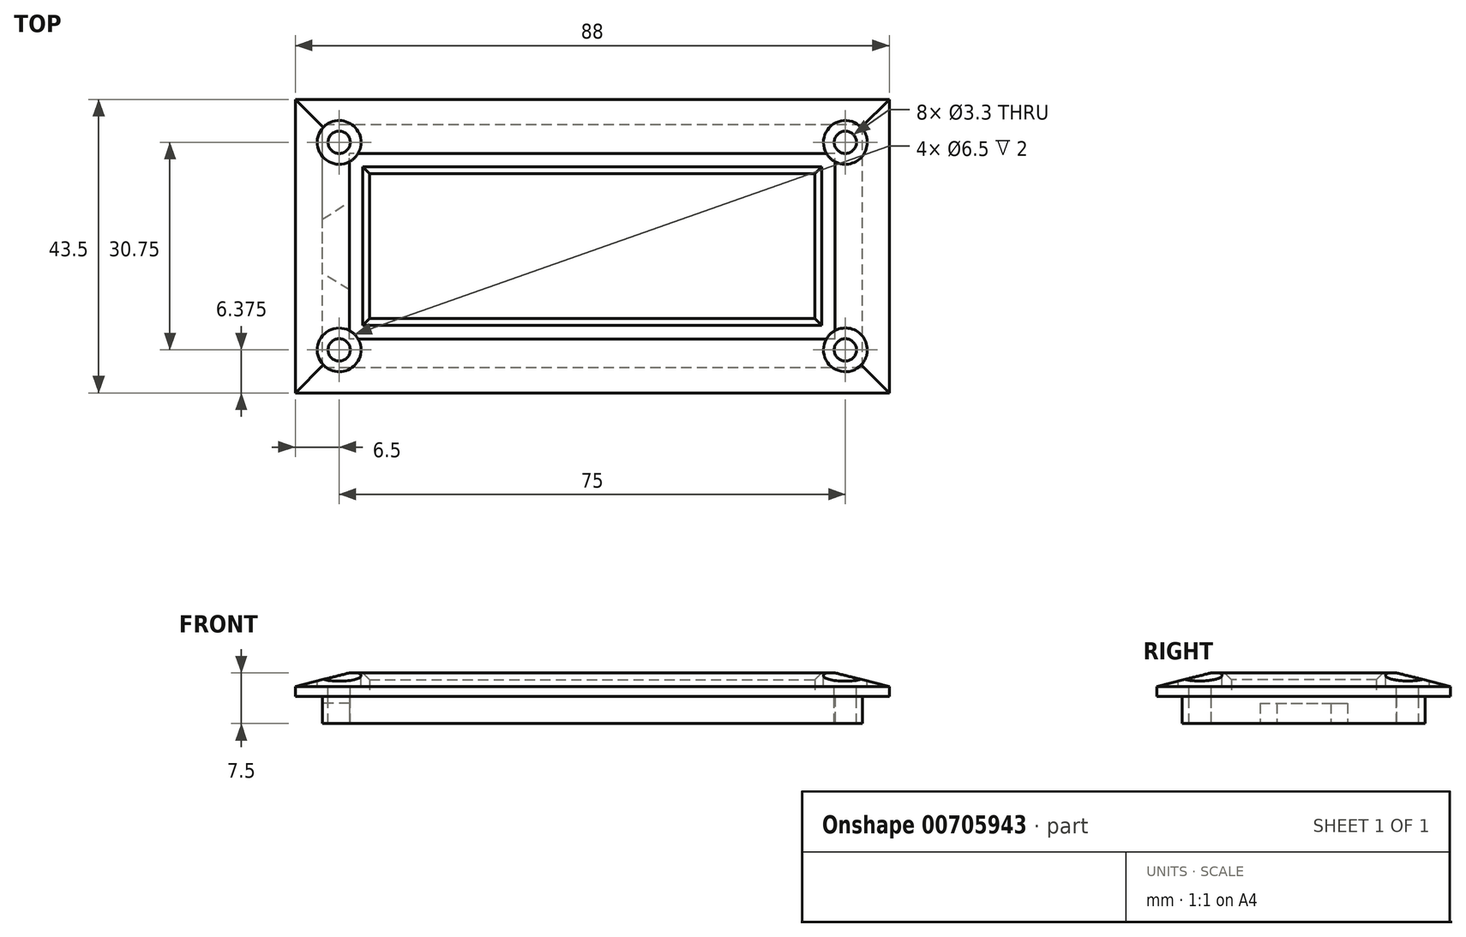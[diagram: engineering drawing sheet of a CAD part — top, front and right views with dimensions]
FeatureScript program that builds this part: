
annotation { "Feature Type Name" : "Feature", "Feature Type Description" : "" }
export const myFeature = defineFeature(function(context is Context, id is Id, definition is map)
    precondition{}
    {
        {
            var Q0;
            Q0=qCreatedBy(makeId("Top.planeOp"),FACE);
            var sketch = newSketch(context, id + "F0", { "sketchPlane" : qUnion([Q0])});
            skLineSegment(sketch, "E0.bottom", {"start": v(36, -13.75) * mm, "end": v(-36, -13.75) * mm});
            skLineSegment(sketch, "E0.top", {"start": v(36, 13.75) * mm, "end": v(-36, 13.75) * mm});
            skLineSegment(sketch, "E0.left", {"start": v(36, -13.75) * mm, "end": v(36, 13.75) * mm});
            skLineSegment(sketch, "E0.right", {"start": v(-36, -13.75) * mm, "end": v(-36, 13.75) * mm});
            skPoint(sketch, "E0.middle", {"position": v(0, 0) * mm});
            skLineSegment(sketch, "E1.bottom", {"start": v(40, -18) * mm, "end": v(-40, -18) * mm});
            skLineSegment(sketch, "E1.top", {"start": v(40, 18) * mm, "end": v(-40, 18) * mm});
            skLineSegment(sketch, "E1.left", {"start": v(40, -18) * mm, "end": v(40, 18) * mm});
            skLineSegment(sketch, "E1.right", {"start": v(-40, -18) * mm, "end": v(-40, 18) * mm});
            skSolve(sketch);
        }
        {
            var Q0;
            Q0=makeQuery(id+"F0.imprint","IMPRINT",FACE,{"disambiguationData":[TD([[makeQuery(id+"F0.imprint","IMPRINT",EDGE,{"derivedFrom":sQuery(id+"F0.wireOp",EDGE,"E0.bottom")}),1.0]])]});
            extrude(context, id + "F1", {"entities" : qUnion([Q0]), "depth" : 4 * mm, "offsetDistance" : 25 * mm});
        }
        {
            var Q0;
            Q0=makeQuery(id+"F1.opExtrude","CAP_FACE",FACE,{"disambiguationData":[OSD([sQuery(id+"F0.wireOp",EDGE,"E0.bottom"),sQuery(id+"F0.wireOp",EDGE,"E0.top"),sQuery(id+"F0.wireOp",EDGE,"E0.left"),sQuery(id+"F0.wireOp",EDGE,"E0.right"),sQuery(id+"F0.wireOp",EDGE,"E1.bottom"),sQuery(id+"F0.wireOp",EDGE,"E1.top"),sQuery(id+"F0.wireOp",EDGE,"E1.left"),sQuery(id+"F0.wireOp",EDGE,"E1.right")])],"isStart":true});
            var sketch = newSketch(context, id + "F2", { "sketchPlane" : qUnion([Q0])});
            skLineSegment(sketch, "E2", {"start": v(-36, 6.5) * mm, "end": v(-40, 4) * mm});
            skLineSegment(sketch, "E3", {"start": v(-40, 4) * mm, "end": v(-40, -4) * mm});
            skLineSegment(sketch, "E4", {"start": v(-40, -4) * mm, "end": v(-36, -6.5) * mm});
            skLineSegment(sketch, "E5", {"start": v(-36, -6.5) * mm, "end": v(-36, 6.5) * mm});
            skSolve(sketch);
        }
        {
            var Q0;
            Q0=makeQuery(id+"F2.imprint","IMPRINT",FACE,{"disambiguationData":[TD([[makeQuery(id+"F2.imprint","IMPRINT",EDGE,{"derivedFrom":sQuery(id+"F2.wireOp",EDGE,"E2")}),1.0]])]});
            extrude(context, id + "F3", {"entities" : qUnion([Q0]), "operationType" : NewBodyOperationType.REMOVE, "oppositeDirection" : true, "depth" : 3 * mm, "offsetDistance" : 25 * mm});
        }
        {
            var Q0;
            Q0=makeQuery(id+"F1.opExtrude","CAP_FACE",FACE,{"disambiguationData":[OSD([sQuery(id+"F0.wireOp",EDGE,"E0.bottom"),sQuery(id+"F0.wireOp",EDGE,"E0.top"),sQuery(id+"F0.wireOp",EDGE,"E0.left"),sQuery(id+"F0.wireOp",EDGE,"E0.right"),sQuery(id+"F0.wireOp",EDGE,"E1.bottom"),sQuery(id+"F0.wireOp",EDGE,"E1.top"),sQuery(id+"F0.wireOp",EDGE,"E1.left"),sQuery(id+"F0.wireOp",EDGE,"E1.right")])],"isStart":false});
            var sketch = newSketch(context, id + "F4", { "sketchPlane" : qUnion([Q0])});
            skLineSegment(sketch, "E6.bottom", {"start": v(37.5, -15.37) * mm, "end": v(-37.5, -15.38) * mm});
            skLineSegment(sketch, "E6.top", {"start": v(37.5, 15.38) * mm, "end": v(-37.5, 15.37) * mm});
            skLineSegment(sketch, "E6.left", {"start": v(37.5, -15.37) * mm, "end": v(37.5, 15.38) * mm});
            skLineSegment(sketch, "E6.right", {"start": v(-37.5, -15.38) * mm, "end": v(-37.5, 15.37) * mm});
            skPoint(sketch, "E6.middle", {"position": v(0, 0) * mm});
            skCircle(sketch, "E7", {"center": v(-37.5, 15.37) * mm, "radius": 1.63 * mm});
            skCircle(sketch, "E8", {"center": v(-37.5, -15.38) * mm, "radius": 1.63 * mm});
            skCircle(sketch, "E9", {"center": v(37.5, -15.37) * mm, "radius": 1.63 * mm});
            skCircle(sketch, "E10", {"center": v(37.5, 15.38) * mm, "radius": 1.63 * mm});
            skSolve(sketch);
        }
        {
            var Q0;
            {var subQ0=sQuery(id+"F4.wireOp",EDGE,"E6.right");var subQ1=sQuery(id+"F4.wireOp",EDGE,"E6.top");var subQ2=makeQuery(id+"F4.imprint","INTERSECT",VERTEX,{"derivedFrom":[subQ1,subQ0]});Q0=makeQuery(id+"F4.imprint","IMPRINT",FACE,{"disambiguationData":[TD([[makeQuery(id+"F4.imprint","IMPRINT",EDGE,{"disambiguationData":[TD([[subQ2,1.0]])],"derivedFrom":subQ1}),1.0]])]});}
            var Q1;
            {var subQ0=sQuery(id+"F4.wireOp",EDGE,"E6.right");var subQ1=sQuery(id+"F4.wireOp",EDGE,"E6.top");var subQ2=makeQuery(id+"F4.imprint","INTERSECT",VERTEX,{"derivedFrom":[subQ1,subQ0]});Q1=makeQuery(id+"F4.imprint","IMPRINT",FACE,{"disambiguationData":[TD([[makeQuery(id+"F4.imprint","IMPRINT",EDGE,{"disambiguationData":[TD([[subQ2,1.0]])],"derivedFrom":subQ1}),-1.0]])]});}
            var Q2;
            {var subQ0=sQuery(id+"F4.wireOp",EDGE,"E6.right");var subQ1=sQuery(id+"F4.wireOp",EDGE,"E6.bottom");var subQ2=makeQuery(id+"F4.imprint","INTERSECT",VERTEX,{"derivedFrom":[subQ1,subQ0]});Q2=makeQuery(id+"F4.imprint","IMPRINT",FACE,{"disambiguationData":[TD([[makeQuery(id+"F4.imprint","IMPRINT",EDGE,{"disambiguationData":[TD([[subQ2,1.0]])],"derivedFrom":subQ1}),1.0]])]});}
            var Q3;
            {var subQ0=sQuery(id+"F4.wireOp",EDGE,"E6.right");var subQ1=sQuery(id+"F4.wireOp",EDGE,"E6.bottom");var subQ2=makeQuery(id+"F4.imprint","INTERSECT",VERTEX,{"derivedFrom":[subQ1,subQ0]});Q3=makeQuery(id+"F4.imprint","IMPRINT",FACE,{"disambiguationData":[TD([[makeQuery(id+"F4.imprint","IMPRINT",EDGE,{"disambiguationData":[TD([[subQ2,1.0]])],"derivedFrom":subQ1}),-1.0]])]});}
            var Q4;
            {var subQ0=sQuery(id+"F4.wireOp",EDGE,"E6.left");var subQ1=sQuery(id+"F4.wireOp",EDGE,"E6.bottom");var subQ2=makeQuery(id+"F4.imprint","INTERSECT",VERTEX,{"derivedFrom":[subQ1,subQ0]});Q4=makeQuery(id+"F4.imprint","IMPRINT",FACE,{"disambiguationData":[TD([[makeQuery(id+"F4.imprint","IMPRINT",EDGE,{"disambiguationData":[TD([[subQ2,-1.0]])],"derivedFrom":subQ1}),1.0]])]});}
            var Q5;
            {var subQ0=sQuery(id+"F4.wireOp",EDGE,"E6.left");var subQ1=sQuery(id+"F4.wireOp",EDGE,"E6.bottom");var subQ2=makeQuery(id+"F4.imprint","INTERSECT",VERTEX,{"derivedFrom":[subQ1,subQ0]});Q5=makeQuery(id+"F4.imprint","IMPRINT",FACE,{"disambiguationData":[TD([[makeQuery(id+"F4.imprint","IMPRINT",EDGE,{"disambiguationData":[TD([[subQ2,-1.0]])],"derivedFrom":subQ1}),-1.0]])]});}
            var Q6;
            {var subQ0=sQuery(id+"F4.wireOp",EDGE,"E6.left");var subQ1=sQuery(id+"F4.wireOp",EDGE,"E6.top");var subQ2=makeQuery(id+"F4.imprint","INTERSECT",VERTEX,{"derivedFrom":[subQ1,subQ0]});Q6=makeQuery(id+"F4.imprint","IMPRINT",FACE,{"disambiguationData":[TD([[makeQuery(id+"F4.imprint","IMPRINT",EDGE,{"disambiguationData":[TD([[subQ2,-1.0]])],"derivedFrom":subQ1}),1.0]])]});}
            var Q7;
            {var subQ0=sQuery(id+"F4.wireOp",EDGE,"E6.left");var subQ1=sQuery(id+"F4.wireOp",EDGE,"E6.top");var subQ2=makeQuery(id+"F4.imprint","INTERSECT",VERTEX,{"derivedFrom":[subQ1,subQ0]});Q7=makeQuery(id+"F4.imprint","IMPRINT",FACE,{"disambiguationData":[TD([[makeQuery(id+"F4.imprint","IMPRINT",EDGE,{"disambiguationData":[TD([[subQ2,-1.0]])],"derivedFrom":subQ1}),-1.0]])]});}
            var Q8;
            Q8=sQuery(id+"F4.wireOp",EDGE,"E7");
            var Q9;
            Q9=sQuery(id+"F4.wireOp",EDGE,"E8");
            var Q10;
            Q10=sQuery(id+"F4.wireOp",EDGE,"E9");
            var Q11;
            Q11=sQuery(id+"F4.wireOp",EDGE,"E10");
            extrude(context, id + "F5", {"entities" : qUnion([Q0, Q1, Q2, Q3, Q4, Q5, Q6, Q7]), "surfaceEntities" : qUnion([Q8, Q9, Q10, Q11]), "endBound" : BoundingType.SYMMETRIC, "depth" : 50 * mm, "offsetDistance" : 25 * mm});
        }
        {
            var Q0;
            Q0=makeQuery(id+"F1.opExtrude","CAP_FACE",FACE,{"disambiguationData":[OSD([sQuery(id+"F0.wireOp",EDGE,"E0.bottom"),sQuery(id+"F0.wireOp",EDGE,"E0.top"),sQuery(id+"F0.wireOp",EDGE,"E0.left"),sQuery(id+"F0.wireOp",EDGE,"E0.right"),sQuery(id+"F0.wireOp",EDGE,"E1.bottom"),sQuery(id+"F0.wireOp",EDGE,"E1.top"),sQuery(id+"F0.wireOp",EDGE,"E1.left"),sQuery(id+"F0.wireOp",EDGE,"E1.right")])],"isStart":false});
            var sketch = newSketch(context, id + "F6", { "sketchPlane" : qUnion([Q0])});
            skLineSegment(sketch, "E11.0", {"start": v(44, -21.75) * mm, "end": v(44, 21.75) * mm});
            skLineSegment(sketch, "E11.1", {"start": v(44, -21.75) * mm, "end": v(-44, -21.75) * mm});
            skLineSegment(sketch, "E11.2", {"start": v(-44, -21.75) * mm, "end": v(-44, 21.75) * mm});
            skLineSegment(sketch, "E11.3", {"start": v(44, 21.75) * mm, "end": v(-44, 21.75) * mm});
            skLineSegment(sketch, "E12.0", {"start": v(-33, -10.75) * mm, "end": v(-33, 10.75) * mm});
            skLineSegment(sketch, "E12.1", {"start": v(33, -10.75) * mm, "end": v(-33, -10.75) * mm});
            skLineSegment(sketch, "E12.2", {"start": v(33, -10.75) * mm, "end": v(33, 10.75) * mm});
            skLineSegment(sketch, "E12.3", {"start": v(33, 10.75) * mm, "end": v(-33, 10.75) * mm});
            skPoint(sketch, "E13.0.end.orphan", {"position": v(-36, 13.75) * mm});
            skPoint(sketch, "E14.0.end.orphan", {"position": v(-36, -13.75) * mm});
            skPoint(sketch, "E15.0.end.orphan", {"position": v(36, 13.75) * mm});
            skPoint(sketch, "E15.0.start.orphan", {"position": v(36, -13.75) * mm});
            skSolve(sketch);
        }
        {
            var Q0;
            Q0=makeQuery(id+"F6.imprint","IMPRINT",FACE,{"disambiguationData":[TD([[makeQuery(id+"F6.imprint","IMPRINT",EDGE,{"derivedFrom":sQuery(id+"F6.wireOp",EDGE,"E11.0")}),1.0]])]});
            var Q1;
            Q1=makeQuery(id+"F6.imprint","IMPRINT",FACE,{"disambiguationData":[TD([[makeQuery(id+"F6.imprint","IMPRINT",EDGE,{"derivedFrom":makeQuery(id+"F1.opExtrude","CAP_EDGE",EDGE,{"disambiguationData":[OSD([sQuery(id+"F0.wireOp",EDGE,"E0.bottom")])],"isStart":false})}),1.0]])]});
            var Q2;
            Q2=makeQuery(id+"F6.imprint","IMPRINT",FACE,{"disambiguationData":[TD([[makeQuery(id+"F6.imprint","IMPRINT",EDGE,{"derivedFrom":sQuery(id+"F6.wireOp",EDGE,"E12.0")}),1.0]])]});
            extrude(context, id + "F7", {"entities" : qUnion([Q0, Q1, Q2]), "depth" : 3.5 * mm, "offsetDistance" : 25 * mm});
        }
        {
            var Q0;
            Q0=makeQuery(id+"F7.opExtrude","CAP_EDGE",EDGE,{"disambiguationData":[OSD([sQuery(id+"F6.wireOp",EDGE,"E11.1")])],"isStart":false});
            var Q1;
            Q1=makeQuery(id+"F7.opExtrude","CAP_EDGE",EDGE,{"disambiguationData":[OSD([sQuery(id+"F6.wireOp",EDGE,"E11.2")])],"isStart":false});
            var Q2;
            Q2=makeQuery(id+"F7.opExtrude","CAP_EDGE",EDGE,{"disambiguationData":[OSD([sQuery(id+"F6.wireOp",EDGE,"E11.3")])],"isStart":false});
            var Q3;
            Q3=makeQuery(id+"F7.opExtrude","CAP_EDGE",EDGE,{"disambiguationData":[OSD([sQuery(id+"F6.wireOp",EDGE,"E11.0")])],"isStart":false});
            chamfer(context, id + "F8", {"entities" : qUnion([Q0, Q1, Q2, Q3]), "chamferType" : ChamferType.TWO_OFFSETS, "width1" : 2 * mm, "oppositeDirection" : false, "width2" : 8 * mm, "tangentPropagation" : true});
        }
        {
            var Q0;
            Q0=makeQuery(id+"F7.opExtrude","CAP_EDGE",EDGE,{"disambiguationData":[OSD([sQuery(id+"F6.wireOp",EDGE,"E12.0")])],"isStart":false});
            var Q1;
            Q1=makeQuery(id+"F7.opExtrude","CAP_EDGE",EDGE,{"disambiguationData":[OSD([sQuery(id+"F6.wireOp",EDGE,"E12.3")])],"isStart":false});
            var Q2;
            Q2=makeQuery(id+"F7.opExtrude","CAP_EDGE",EDGE,{"disambiguationData":[OSD([sQuery(id+"F6.wireOp",EDGE,"E12.2")])],"isStart":false});
            var Q3;
            Q3=makeQuery(id+"F7.opExtrude","CAP_EDGE",EDGE,{"disambiguationData":[OSD([sQuery(id+"F6.wireOp",EDGE,"E12.1")])],"isStart":false});
            chamfer(context, id + "F9", {"entities" : qUnion([Q0, Q1, Q2, Q3]), "width" : 1 * mm, "tangentPropagation" : true});
        }
        {
            var Q0;
            Q0=makeQuery(id+"F7.opExtrude","CAP_FACE",FACE,{"disambiguationData":[OSD([sQuery(id+"F6.wireOp",EDGE,"E11.0"),sQuery(id+"F6.wireOp",EDGE,"E11.1"),sQuery(id+"F6.wireOp",EDGE,"E11.2"),sQuery(id+"F6.wireOp",EDGE,"E11.3"),sQuery(id+"F6.wireOp",EDGE,"E12.0"),sQuery(id+"F6.wireOp",EDGE,"E12.1"),sQuery(id+"F6.wireOp",EDGE,"E12.2"),sQuery(id+"F6.wireOp",EDGE,"E12.3")])],"isStart":false});
            var sketch = newSketch(context, id + "F10", { "sketchPlane" : qUnion([Q0])});
            skPoint(sketch, "E16.0", {"position": v(-37.5, 15.37) * mm});
            skPoint(sketch, "E17.0", {"position": v(-37.5, -15.38) * mm});
            skPoint(sketch, "E18.0", {"position": v(37.5, -15.37) * mm});
            skPoint(sketch, "E19.0", {"position": v(37.5, 15.38) * mm});
            skSolve(sketch);
        }
        {
            var Q0;
            Q0=sQuery(id+"F10.wireOp",VERTEX,"E19.0");
            var Q1;
            Q1=sQuery(id+"F10.wireOp",VERTEX,"E18.0");
            var Q2;
            Q2=sQuery(id+"F10.wireOp",VERTEX,"E17.0");
            var Q3;
            Q3=sQuery(id+"F10.wireOp",VERTEX,"E16.0");
            var Q4;
            Q4=makeQuery(id+"F1.opExtrude","SWEPT_BODY",BODY,{"disambiguationData":[OSD([sQuery(id+"F0.wireOp",EDGE,"E0.bottom"),sQuery(id+"F0.wireOp",EDGE,"E0.top"),sQuery(id+"F0.wireOp",EDGE,"E0.left"),sQuery(id+"F0.wireOp",EDGE,"E0.right"),sQuery(id+"F0.wireOp",EDGE,"E1.bottom"),sQuery(id+"F0.wireOp",EDGE,"E1.top"),sQuery(id+"F0.wireOp",EDGE,"E1.left"),sQuery(id+"F0.wireOp",EDGE,"E1.right")])]});
            var Q5;
            Q5=makeQuery(id+"F7.opExtrude","SWEPT_BODY",BODY,{"disambiguationData":[OSD([sQuery(id+"F6.wireOp",EDGE,"E11.0"),sQuery(id+"F6.wireOp",EDGE,"E11.1"),sQuery(id+"F6.wireOp",EDGE,"E11.2"),sQuery(id+"F6.wireOp",EDGE,"E11.3"),sQuery(id+"F6.wireOp",EDGE,"E12.0"),sQuery(id+"F6.wireOp",EDGE,"E12.1"),sQuery(id+"F6.wireOp",EDGE,"E12.2"),sQuery(id+"F6.wireOp",EDGE,"E12.3")])]});
            hole(context, id + "F11", {"style" : HoleStyle.C_BORE, "endStyle" : HoleEndStyle.THROUGH, "holeDiameter" : 3.3 * mm, "cBoreDiameter" : 6.5 * mm, "cBoreDepth" : 2 * mm, "majorDiameter" : 5 * mm, "isTappedThrough" : true, "tappedDepth" : 12 * mm, "tapClearance" : 3, "startFromSketch" : true, "locations" : qUnion([Q0, Q1, Q2, Q3]), "scope" : qUnion([Q4, Q5])});
        }
        {
            var Q0;
            Q0=makeQuery(id+"F5.opExtrude","SWEPT_BODY",BODY,{"disambiguationData":[OSD([sQuery(id+"F4.wireOp",EDGE,"E7")])]});
            var Q1;
            Q1=makeQuery(id+"F5.opExtrude","SWEPT_BODY",BODY,{"disambiguationData":[OSD([sQuery(id+"F4.wireOp",EDGE,"E8")])]});
            var Q2;
            Q2=makeQuery(id+"F5.opExtrude","SWEPT_BODY",BODY,{"disambiguationData":[OSD([sQuery(id+"F4.wireOp",EDGE,"E9")])]});
            var Q3;
            Q3=makeQuery(id+"F5.opExtrude","SWEPT_BODY",BODY,{"disambiguationData":[OSD([sQuery(id+"F4.wireOp",EDGE,"E10")])]});
            var Q4;
            Q4=makeQuery(id+"F1.opExtrude","SWEPT_BODY",BODY,{"disambiguationData":[OSD([sQuery(id+"F0.wireOp",EDGE,"E0.bottom"),sQuery(id+"F0.wireOp",EDGE,"E0.top"),sQuery(id+"F0.wireOp",EDGE,"E0.left"),sQuery(id+"F0.wireOp",EDGE,"E0.right"),sQuery(id+"F0.wireOp",EDGE,"E1.bottom"),sQuery(id+"F0.wireOp",EDGE,"E1.top"),sQuery(id+"F0.wireOp",EDGE,"E1.left"),sQuery(id+"F0.wireOp",EDGE,"E1.right")])]});
            var Q5;
            Q5=makeQuery(id+"F7.opExtrude","SWEPT_BODY",BODY,{"disambiguationData":[OSD([sQuery(id+"F6.wireOp",EDGE,"E11.0"),sQuery(id+"F6.wireOp",EDGE,"E11.1"),sQuery(id+"F6.wireOp",EDGE,"E11.2"),sQuery(id+"F6.wireOp",EDGE,"E11.3"),sQuery(id+"F6.wireOp",EDGE,"E12.0"),sQuery(id+"F6.wireOp",EDGE,"E12.1"),sQuery(id+"F6.wireOp",EDGE,"E12.2"),sQuery(id+"F6.wireOp",EDGE,"E12.3")])]});
            booleanBodies(context, id + "F12", {"operationType" : BooleanOperationType.SUBTRACTION, "tools" : qUnion([Q0, Q1, Q2, Q3]), "targets" : qUnion([Q4, Q5])});
        }
    });
